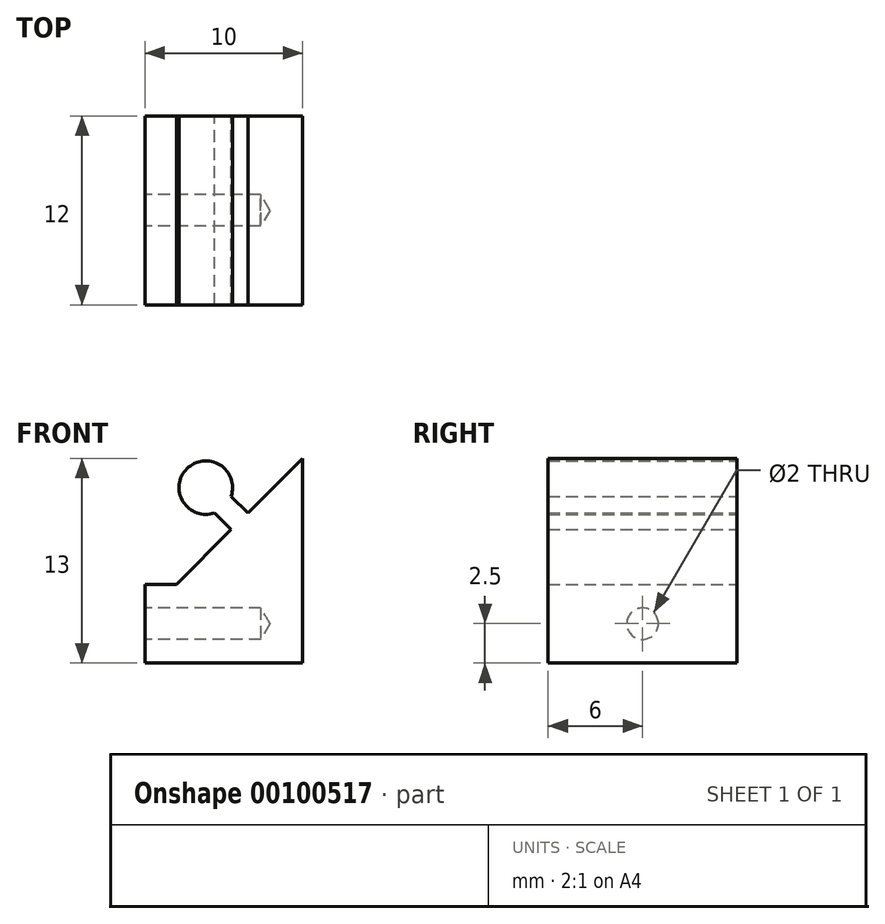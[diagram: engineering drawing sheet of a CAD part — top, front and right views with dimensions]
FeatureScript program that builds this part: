
annotation { "Feature Type Name" : "Feature", "Feature Type Description" : "" }
export const myFeature = defineFeature(function(context is Context, id is Id, definition is map)
    precondition{}
    {
        {
            var Q0;
            Q0=qCreatedBy(makeId("Front.planeOp"),FACE);
            var sketch = newSketch(context, id + "F0", { "sketchPlane" : qUnion([Q0])});
            skLineSegment(sketch, "E0", {"start": v(0, 0) * mm, "end": v(-10, 0) * mm});
            skLineSegment(sketch, "E1", {"start": v(-10, 0) * mm, "end": v(-10, 5) * mm});
            skLineSegment(sketch, "E2", {"start": v(-10, 5) * mm, "end": v(-8, 5) * mm});
            skLineSegment(sketch, "E3", {"start": v(-8, 5) * mm, "end": v(-4.53, 8.47) * mm});
            skLineSegment(sketch, "E4", {"start": v(0, 13) * mm, "end": v(0, 0) * mm});
            skLineSegment(sketch, "E5", {"start": v(-4.53, 8.47) * mm, "end": v(-5.6, 9.53) * mm});
            skLineSegment(sketch, "E6", {"start": v(-3.47, 9.53) * mm, "end": v(-4.53, 10.6) * mm});
            skArc(sketch, "E7", {"start": v(-4.53, 10.6) * mm, "mid": v(-7.34, 12.34) * mm, "end": v(-5.6, 9.53) * mm});
            skLineSegment(sketch, "E8", {"start": v(-3.47, 9.53) * mm, "end": v(0, 13) * mm});
            skSolve(sketch);
        }
        {
            var Q0;
            Q0 = qSketchRegion(id + "F0", true);
            extrude(context, id + "F1", {"entities" : qUnion([Q0]), "depth" : 12 * mm});
        }
        {
            var Q0;
            Q0=makeQuery(id+"F1.opExtrude","SWEPT_FACE",FACE,{"disambiguationData":[OSD([sQuery(id+"F0.wireOp",EDGE,"E1")])]});
            var sketch = newSketch(context, id + "F2", { "sketchPlane" : qUnion([Q0])});
            skPoint(sketch, "E9", {"position": v(6, 2.5) * mm});
            skSolve(sketch);
        }
        {
            var Q0;
            Q0=sQuery(id+"F2.wireOp",VERTEX,"E9");
            var Q1;
            Q1=makeQuery(id+"F1.opExtrude","SWEPT_BODY",BODY,{"disambiguationData":[OSD([sQuery(id+"F0.wireOp",EDGE,"E0"),sQuery(id+"F0.wireOp",EDGE,"E1"),sQuery(id+"F0.wireOp",EDGE,"E2"),sQuery(id+"F0.wireOp",EDGE,"E3"),sQuery(id+"F0.wireOp",EDGE,"E4"),sQuery(id+"F0.wireOp",EDGE,"E5"),sQuery(id+"F0.wireOp",EDGE,"E6"),sQuery(id+"F0.wireOp",EDGE,"E7"),sQuery(id+"F0.wireOp",EDGE,"E8")])]});
            hole(context, id + "F3", {"style" : HoleStyle.SIMPLE, "endStyle" : HoleEndStyle.BLIND, "holeDiameter" : 2 * mm, "holeDepth" : 7.34 * mm, "locations" : qUnion([Q0]), "scope" : qUnion([Q1])});
        }
    });
